# Revit family: Electrical_Equipment-Floor_Box-Hubbell_Wiring-CFBS1R4SFB_CR
name_source: partatom
category: Electrical Fixtures
revit_build: Autodesk Revit 2015 (Build: 20140606_1530(x64)
units: mm (PartAtom-declared; Revit-internal decimal feet)

## types (2) — shared parameters
Assembly Code = D5020115
Conduit Connector 1 Radius = 0.625 "
Conduit Connector 2 Radius = 0.625 "
Conduit Connector_1 Description = 0.75in. 1in. or 1.25in. Data Conduit Connector 1
Conduit Connector_2 Description = 0.75in. 1in or 1.25in. Data Conduit Connector 2
Conduit Connector_3 Description = 0.75in. 1in. or 1.25in. Power Conduit Connector 1
Conduit Connector_4 Description = 0.75in. 1in. or 1.25in. Power Conduit Connector 2
Default Elevation = 48 "
Description = Steel Metal Concrete Recessed Floor box,  4in. Round Cover
Manufacturer = Hubbell Wiring Device
Product Documentation Link = http://www.hubbell-wiring.com
Product Page URL = http://www.hubbell-wiring.com
Product data url = https://bimobject.com
URL = http://www.hubbell-wiring.com

## per-type parameters (varying)
| type | Product Material |
| CFBS1R4SFB | Metal-Hubbell-Steel |
| CFBS1R4SFBCR | Metal-Hubbell-Green Finish |

note: column(s) folded — value = type name in every type: Model

## geometry (parser evidence)
native form markers: Blend x42, Sweep x5
no freeform markers — native parametric forms only
